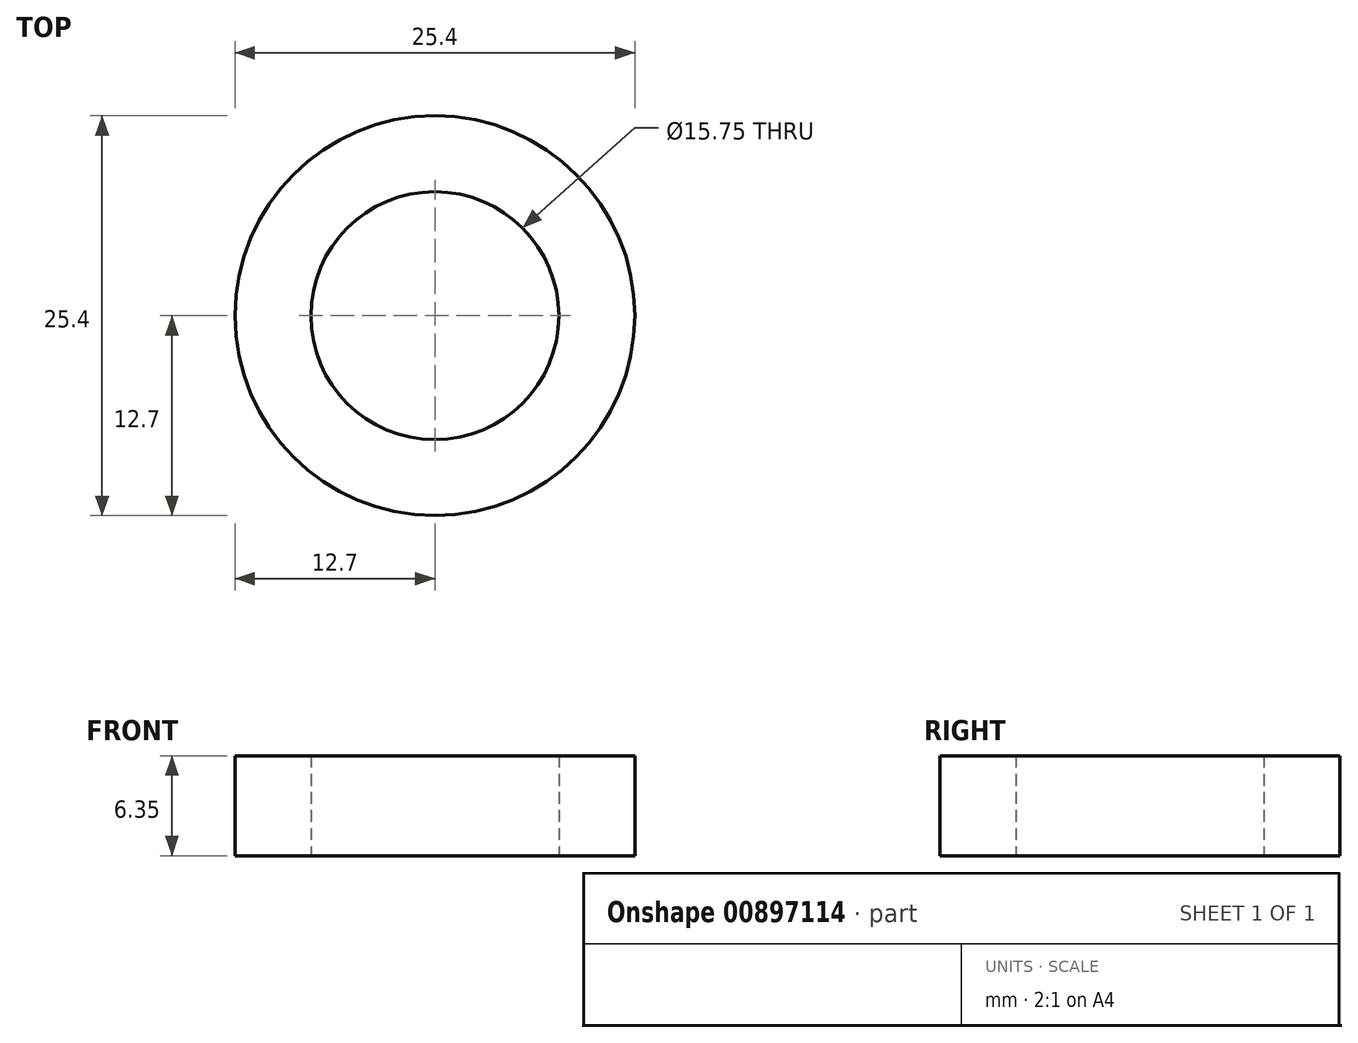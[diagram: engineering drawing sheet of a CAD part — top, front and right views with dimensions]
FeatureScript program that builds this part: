
annotation { "Feature Type Name" : "Feature", "Feature Type Description" : "" }
export const myFeature = defineFeature(function(context is Context, id is Id, definition is map)
    precondition{}
    {
        {
            var Q0;
            Q0=qCreatedBy(makeId("Top.planeOp"),FACE);
            var sketch = newSketch(context, id + "F0", { "sketchPlane" : qUnion([Q0])});
            skCircle(sketch, "E0", {"center": v(0, 0) * mm, "radius": 7.87 * mm});
            skCircle(sketch, "E1", {"center": v(0, 0) * mm, "radius": 12.7 * mm});
            skSolve(sketch);
        }
        {
            var Q0;
            Q0=qSketchRegion(id+"F0",true);
            extrude(context, id + "F1", {"entities" : qUnion([Q0]), "depth" : 6.35 * mm});
        }
    });
